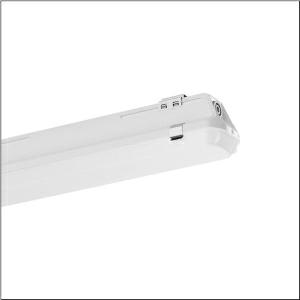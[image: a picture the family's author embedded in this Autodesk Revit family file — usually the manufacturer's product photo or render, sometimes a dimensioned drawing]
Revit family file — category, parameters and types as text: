
# Revit family: monsun_r__11_51fp20mp4b0q_9e0e
name_source: partatom
category: Lighting Fixtures
units: mm (PartAtom-declared; Revit-internal decimal feet)

## family parameters
Cut with Voids When Loaded = No
Host = Face
Light Source = No
Part Type = Normal
Room Calculation Point = No
Round Connector Dimension = Use Diameter
Shared = No

## types (1)
- --- (1 x LED, 10910 lm, 66.2 W, 4000K)
    Apparent Load = 66 VA
    CIE Flux Codes = 45 75 93 94 100
    Color Rendering = 80
    Color Temperature = 4000K
    Default Elevation = 1800 mm
    Description = Monsun® 11, damp-proof luminaire, chain hanger, primary optical cover: enclosure, of PC, light emission: direct distribution, primary light characteristic: symmetric, installation type: suspended mounting, surface-mounted, horizontal mounting, vertical mounting, LED, rated luminous flux: 10.910lm, luminous efficacy: 165lm/W, light colour: 840, colour temperature: 4000K, control gear: ECG, with terminal, 3-pole, max. 2.5mm², mains connection: 220..240V, AC, 50/60Hz, rated input power: 66W, luminaire housing, of glass-fibre reinforced polyester, uncoated, bright grey, incl. chain hanger, length: 1.590mm, width: 90mm, height: 88mm, clip for enclosure, of stainless steel (V2A), ceiling mounting element, of stainless steel (V2A), chain hanger, of stainless steel (V2A), protection rating (complete): IP66, insulation class (complete): insulation class I (protective earthing), certification: CE, ENEC, VDE, UKCA, protection symbol: D, impact resistance: IK08, permissible operating ambient temperature: -35..+35°C, standard: EN 50419, EN 60598-2-1, no direct snow, no direct sun, no direct rain, for indoor or canopied outdoor use, corresponds to IFS (International Featured Standards) requirements for safety and quality in the food industry, contact your sales advisor before using the luminaires in applications with unclear chemical exposure, large temperature fluctuations or condensation-forming humidity, LABS conformity tested according to VDMA 24364:2018-05, packaging unit: 1 piece
    Height = 89 mm
    Lamp = 1 x LED
    Lamp Light Flux = 10910 lm
    Lamp Power = 66.2 W
    Lamp count = 1
    Length = 1590 mm
    Luminous efficacy = 165 lm/W
    Manufacturer = Siteco
    ModVariant = No
    Model = 51FP20MP4B0Q
    Mounting Place = Ceiling
    Mounting Type = Surface mounted
    Number of Poles = 1
    OnlyDefault = Yes
    Power Factor = 1
    Product Name = Monsun® 11
    Product group = damp-proof luminaire
    ProductGroupID = 300
    Protection Class = Protection class I
    Protection Degree = IP 66
    RLX_Detail_Level = 1
    RLX_Emergency_Light_Flux = 0 lm
    RLX_Emergency_Type = 0
    RLX_Emergency_Type_DB = No
    RlxData = <blob elided: 89937 chars, md5=a94f30bc>
    Socket = socket
    Standby Power = 0 W
    System Light Flux = 10910 lm
    System Power = 66 W
    Type Comments = factory setting: luminous flux: 100 % | (A | C | E) | 155 mA
    Type Image = l_1004748.jpg
    URL = http://relux.com
    VarID = @adj_140503
    Voltage = 0 V
    Weight = 0.00 kg
    Width = 90 mm

## geometry (parser evidence)
native form markers: Blend x4, Sweep x15
no freeform markers — native parametric forms only
